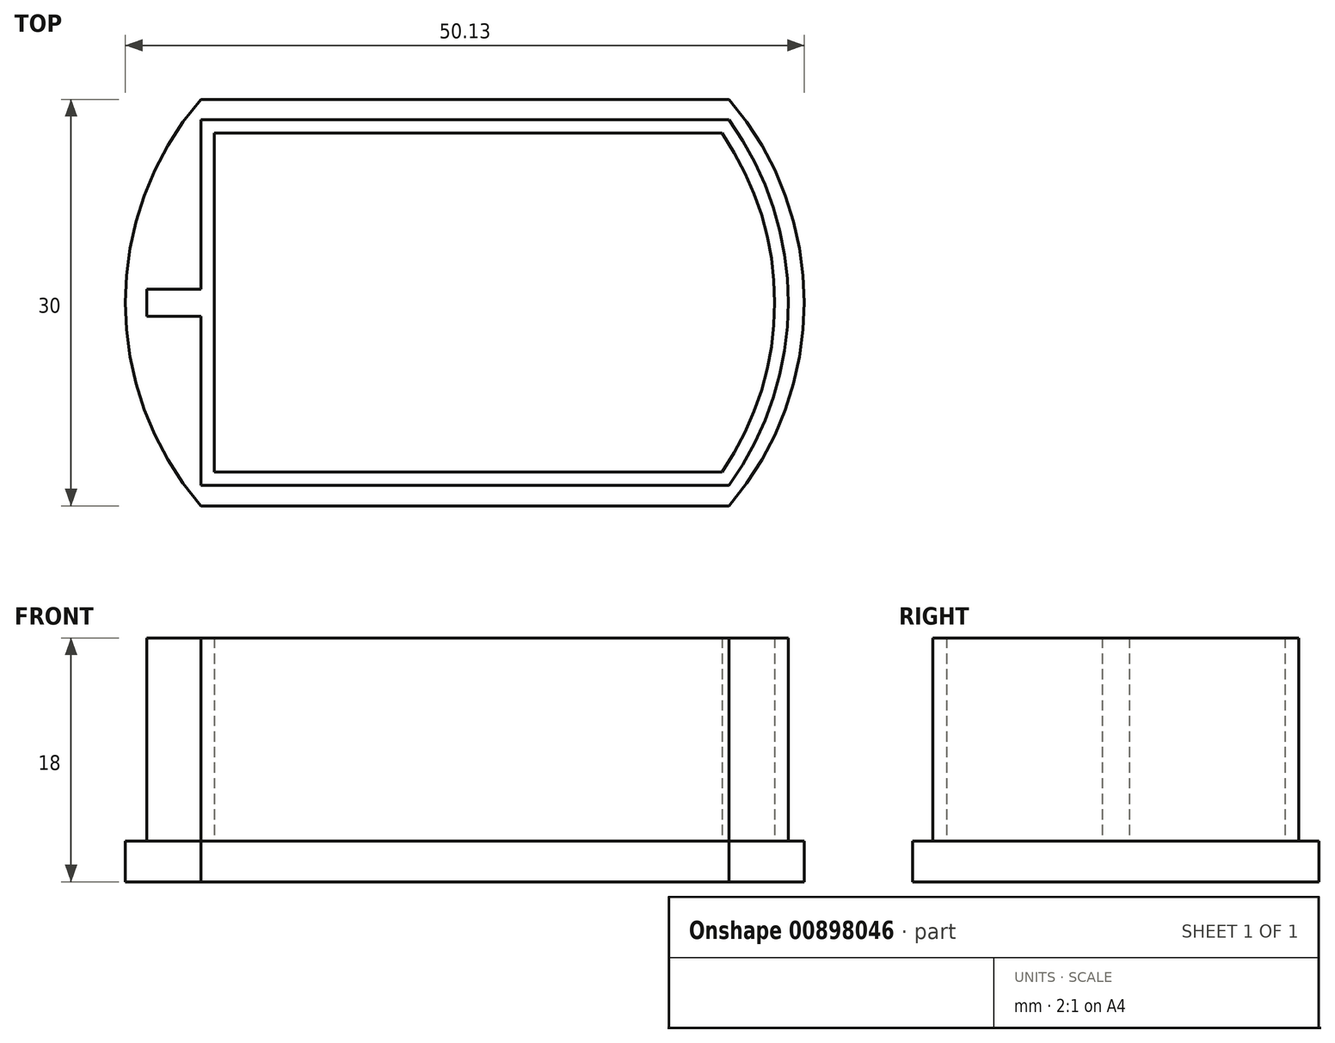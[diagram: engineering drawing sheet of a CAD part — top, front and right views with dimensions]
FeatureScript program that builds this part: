
annotation { "Feature Type Name" : "Feature", "Feature Type Description" : "" }
export const myFeature = defineFeature(function(context is Context, id is Id, definition is map)
    precondition{}
    {
        {
            var Q0;
            Q0=qCreatedBy(makeId("Top.planeOp"),FACE);
            var sketch = newSketch(context, id + "F0", { "sketchPlane" : qUnion([Q0])});
            skLineSegment(sketch, "E0", {"start": v(26.43, 15) * mm, "end": v(-12.57, 15) * mm});
            skLineSegment(sketch, "E1", {"start": v(-12.57, -15) * mm, "end": v(26.43, -15) * mm});
            skArc(sketch, "E2", {"start": v(-12.57, 15) * mm, "mid": v(-18.14, 0) * mm, "end": v(-12.57, -15) * mm});
            skArc(sketch, "E3", {"start": v(26.43, -15) * mm, "mid": v(31.99, 0) * mm, "end": v(26.43, 15) * mm});
            skLineSegment(sketch, "E4", {"start": v(-12.57, 13.5) * mm, "end": v(26.43, 13.5) * mm});
            skLineSegment(sketch, "E5", {"start": v(-12.57, -13.5) * mm, "end": v(26.43, -13.5) * mm});
            skArc(sketch, "E6", {"start": v(26.43, -13.5) * mm, "mid": v(30.8, 0) * mm, "end": v(26.43, 13.5) * mm});
            skLineSegment(sketch, "E7", {"start": v(-12.57, 13.5) * mm, "end": v(-12.57, 1) * mm});
            skLineSegment(sketch, "E8", {"start": v(-12.57, 1) * mm, "end": v(-16.57, 1) * mm});
            skLineSegment(sketch, "E9", {"start": v(-16.57, 1) * mm, "end": v(-16.57, -1) * mm});
            skLineSegment(sketch, "E10", {"start": v(-16.57, -1) * mm, "end": v(-12.57, -1) * mm});
            skLineSegment(sketch, "E11", {"start": v(-12.57, -1) * mm, "end": v(-12.57, -13.5) * mm});
            skSolve(sketch);
        }
        {
            var Q0;
            Q0=makeQuery(id+"F0.imprint","IMPRINT",FACE,{"disambiguationData":[TD([[makeQuery(id+"F0.imprint","IMPRINT",EDGE,{"derivedFrom":sQuery(id+"F0.wireOp",EDGE,"E0")}),1.0]])]});
            var Q1;
            Q1=makeQuery(id+"F0.imprint","IMPRINT",FACE,{"disambiguationData":[TD([[makeQuery(id+"F0.imprint","IMPRINT",EDGE,{"derivedFrom":sQuery(id+"F0.wireOp",EDGE,"E4")}),-1.0]])]});
            extrude(context, id + "F1", {"entities" : qUnion([Q0, Q1]), "depth" : 3 * mm, "offsetDistance" : 25 * mm});
        }
        {
            var Q0;
            Q0=makeQuery(id+"F1.opExtrude","CAP_FACE",FACE,{"disambiguationData":[OSD([sQuery(id+"F0.wireOp",EDGE,"E0"),sQuery(id+"F0.wireOp",EDGE,"E1"),sQuery(id+"F0.wireOp",EDGE,"E2"),sQuery(id+"F0.wireOp",EDGE,"E3")])],"isStart":false});
            var sketch = newSketch(context, id + "F2", { "sketchPlane" : qUnion([Q0])});
            skLineSegment(sketch, "E12", {"start": v(26.43, 15) * mm, "end": v(-12.57, 15) * mm});
            skLineSegment(sketch, "E13", {"start": v(-12.57, -15) * mm, "end": v(26.43, -15) * mm});
            skArc(sketch, "E14", {"start": v(-12.57, 15) * mm, "mid": v(-18.14, 0) * mm, "end": v(-12.57, -15) * mm});
            skArc(sketch, "E15", {"start": v(26.43, -15) * mm, "mid": v(31.99, 0) * mm, "end": v(26.43, 15) * mm});
            skLineSegment(sketch, "E16", {"start": v(-12.57, 13.5) * mm, "end": v(26.43, 13.5) * mm});
            skLineSegment(sketch, "E17", {"start": v(-12.57, -13.5) * mm, "end": v(26.43, -13.5) * mm});
            skArc(sketch, "E18", {"start": v(26.43, -13.5) * mm, "mid": v(30.8, 0) * mm, "end": v(26.43, 13.5) * mm});
            skLineSegment(sketch, "E19", {"start": v(-12.57, 13.5) * mm, "end": v(-12.57, 1) * mm});
            skLineSegment(sketch, "E20", {"start": v(-12.57, 1) * mm, "end": v(-16.57, 1) * mm});
            skLineSegment(sketch, "E21", {"start": v(-16.57, 1) * mm, "end": v(-16.57, -1) * mm});
            skLineSegment(sketch, "E22", {"start": v(-16.57, -1) * mm, "end": v(-12.57, -1) * mm});
            skLineSegment(sketch, "E23", {"start": v(-12.57, -1) * mm, "end": v(-12.57, -13.5) * mm});
            skLineSegment(sketch, "E24.0", {"start": v(-11.57, 12.5) * mm, "end": v(-11.57, 0) * mm});
            skLineSegment(sketch, "E24.1", {"start": v(-11.57, 12.5) * mm, "end": v(25.9, 12.5) * mm});
            skArc(sketch, "E24.3", {"start": v(25.9, -12.5) * mm, "mid": v(29.8, 0) * mm, "end": v(25.9, 12.5) * mm});
            skLineSegment(sketch, "E24.6", {"start": v(-11.57, 0) * mm, "end": v(-11.57, -12.5) * mm});
            skLineSegment(sketch, "E24.7", {"start": v(-11.57, -12.5) * mm, "end": v(25.9, -12.5) * mm});
            skArc(sketch, "E25.0", {"start": v(-14.74, 20) * mm, "mid": v(-23.14, 0) * mm, "end": v(-14.74, -20) * mm});
            skLineSegment(sketch, "E25.1", {"start": v(28.59, 20) * mm, "end": v(-14.74, 20) * mm});
            skArc(sketch, "E25.2", {"start": v(28.59, -20) * mm, "mid": v(36.99, 0) * mm, "end": v(28.59, 20) * mm});
            skLineSegment(sketch, "E25.3", {"start": v(-14.74, -20) * mm, "end": v(28.59, -20) * mm});
            skSolve(sketch);
        }
        {
            var Q0;
            Q0=makeQuery(id+"F2.imprint","IMPRINT",FACE,{"disambiguationData":[TD([[makeQuery(id+"F2.imprint","IMPRINT",EDGE,{"derivedFrom":sQuery(id+"F2.wireOp",EDGE,"E16")}),-1.0]])]});
            extrude(context, id + "F3", {"entities" : qUnion([Q0]), "operationType" : NewBodyOperationType.ADD, "depth" : 15 * mm, "offsetDistance" : 25 * mm});
        }
    });
